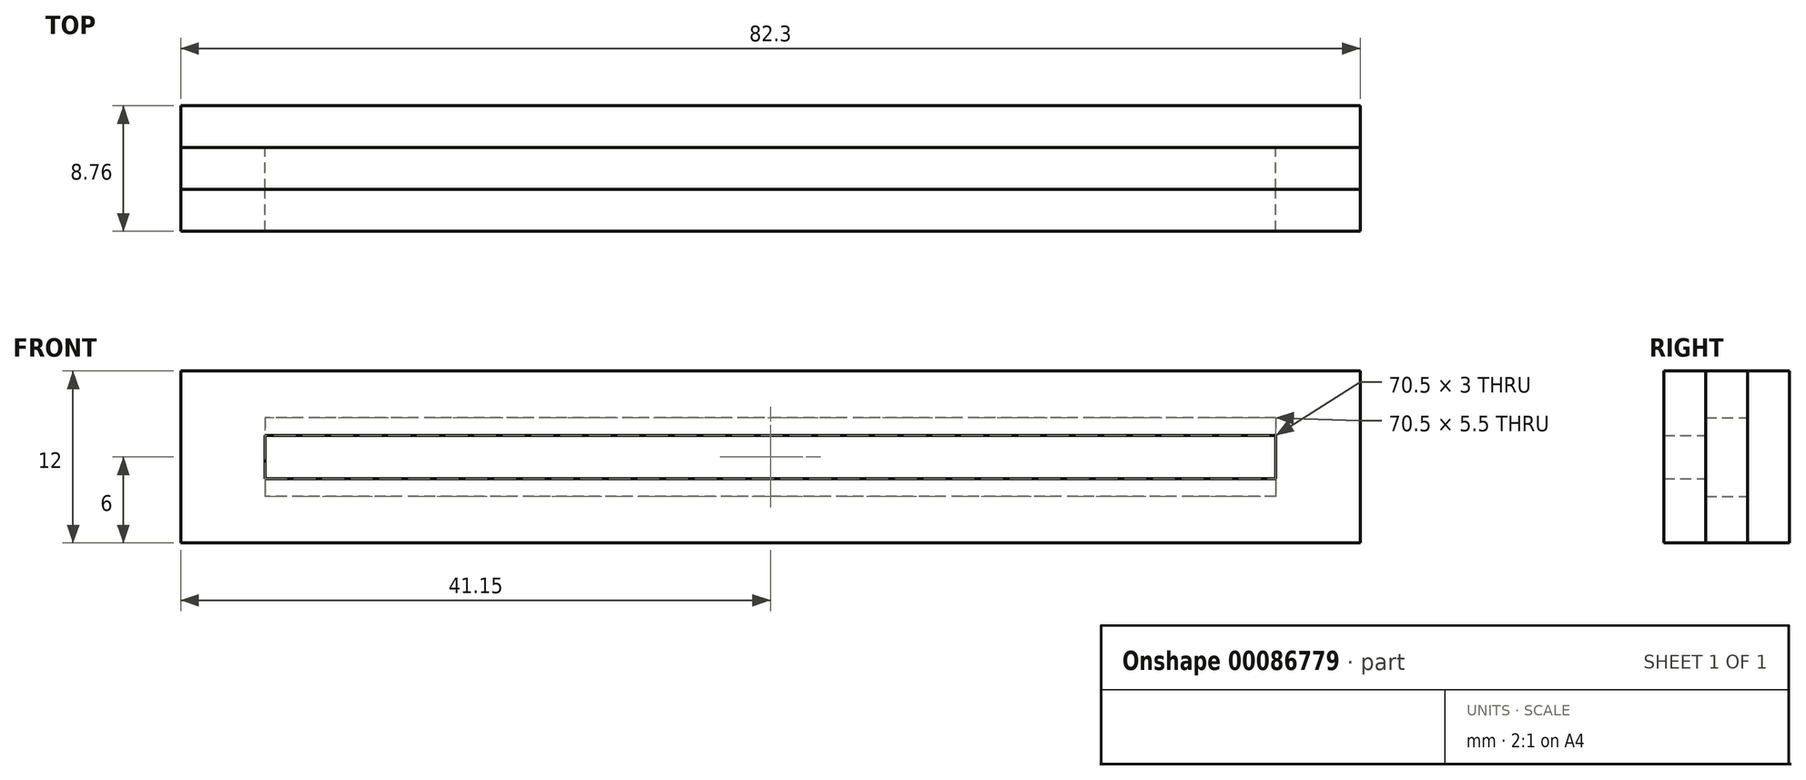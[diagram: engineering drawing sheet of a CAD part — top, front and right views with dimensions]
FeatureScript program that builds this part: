
annotation { "Feature Type Name" : "Feature", "Feature Type Description" : "" }
export const myFeature = defineFeature(function(context is Context, id is Id, definition is map)
    precondition{}
    {
        {
            var Q0;
            Q0=qCreatedBy(makeId("Front.planeOp"),FACE);
            var sketch = newSketch(context, id + "F0", { "sketchPlane" : qUnion([Q0])});
            skLineSegment(sketch, "E0.bottom", {"start": v(41.15, 6) * mm, "end": v(-41.15, 6) * mm});
            skLineSegment(sketch, "E0.top", {"start": v(41.15, -6) * mm, "end": v(-41.15, -6) * mm});
            skLineSegment(sketch, "E0.left", {"start": v(41.15, 6) * mm, "end": v(41.15, -6) * mm});
            skLineSegment(sketch, "E0.right", {"start": v(-41.15, 6) * mm, "end": v(-41.15, -6) * mm});
            skSolve(sketch);
        }
        {
            var Q0;
            {var subQ0=sQuery(id+"F0.wireOp",EDGE,"c4q2wAaf-wQR1-omqj-YX6Q-xsGUEn6AxWBf.bottom");Q0=makeQuery(id+"F0.imprint","IMPRINT",FACE,{"disambiguationData":[TD([[makeQuery(id+"F0.imprint","IMPRINT",EDGE,{"derivedFrom":subQ0}),1.0]])]});}
            var Q1;
            {var subQ0=sQuery(id+"F0.wireOp",EDGE,"c4q2wAaf-wQR1-omqj-YX6Q-xsGUEn6AxWBf.top");Q1=makeQuery(id+"F0.imprint","IMPRINT",FACE,{"disambiguationData":[TD([[makeQuery(id+"F0.imprint","IMPRINT",EDGE,{"derivedFrom":subQ0}),-1.0]])]});}
            var Q2;
            Q2=makeQuery(id+"F0.imprint","IMPRINT",FACE,{"disambiguationData":[TD([[makeQuery(id+"F0.imprint","IMPRINT",EDGE,{"derivedFrom":sQuery(id+"F0.wireOp",EDGE,"E0.bottom")}),1.0]])]});
            var Q3;
            Q3=makeQuery(id+"F0.imprint","IMPRINT",FACE,{"disambiguationData":[TD([[makeQuery(id+"F0.imprint","IMPRINT",EDGE,{"derivedFrom":sQuery(id+"F0.wireOp",EDGE,"rwk2xs3n-fW5y-CHEW-mY1I-GiypznhDuFsC.bottom")}),-1.0]])]});
            extrude(context, id + "F1", {"entities" : qUnion([Q0, Q1, Q2, Q3]), "depth" : 2.92 * mm});
        }
        {
            var Q0;
            Q0=makeQuery(id+"F1.opExtrude","CAP_FACE",FACE,{"disambiguationData":[OSD([sQuery(id+"F0.wireOp",EDGE,"E0.bottom"),sQuery(id+"F0.wireOp",EDGE,"E0.top"),sQuery(id+"F0.wireOp",EDGE,"E0.left"),sQuery(id+"F0.wireOp",EDGE,"E0.right")])],"isStart":false});
            var sketch = newSketch(context, id + "F2", { "sketchPlane" : qUnion([Q0])});
            skLineSegment(sketch, "E1.bottom", {"start": v(35.25, 2.75) * mm, "end": v(-35.25, 2.75) * mm});
            skLineSegment(sketch, "E1.top", {"start": v(35.25, -2.75) * mm, "end": v(-35.25, -2.75) * mm});
            skLineSegment(sketch, "E1.left", {"start": v(35.25, 2.75) * mm, "end": v(35.25, -2.75) * mm});
            skLineSegment(sketch, "E1.right", {"start": v(-35.25, 2.75) * mm, "end": v(-35.25, -2.75) * mm});
            skPoint(sketch, "E1.middle", {"position": v(0, 0) * mm});
            skSolve(sketch);
        }
        {
            var Q0;
            Q0=makeQuery(id+"F2.imprint","IMPRINT",FACE,{"disambiguationData":[TD([[makeQuery(id+"F2.imprint","IMPRINT",EDGE,{"derivedFrom":sQuery(id+"F2.wireOp",EDGE,"E1.bottom")}),-1.0]])]});
            extrude(context, id + "F3", {"entities" : qUnion([Q0]), "depth" : 2.92 * mm});
        }
        {
            var Q0;
            Q0=makeQuery(id+"F3.opExtrude","CAP_FACE",FACE,{"disambiguationData":[OSD([sQuery(id+"F0.wireOp",EDGE,"E0.bottom"),sQuery(id+"F0.wireOp",EDGE,"E0.top"),sQuery(id+"F0.wireOp",EDGE,"E0.left"),sQuery(id+"F0.wireOp",EDGE,"E0.right"),sQuery(id+"F2.wireOp",EDGE,"E1.bottom"),sQuery(id+"F2.wireOp",EDGE,"E1.top"),sQuery(id+"F2.wireOp",EDGE,"E1.left"),sQuery(id+"F2.wireOp",EDGE,"E1.right")])],"isStart":false});
            var sketch = newSketch(context, id + "F4", { "sketchPlane" : qUnion([Q0])});
            skLineSegment(sketch, "E2.bottom", {"start": v(35.25, -1.5) * mm, "end": v(-35.25, -1.5) * mm});
            skLineSegment(sketch, "E2.top", {"start": v(35.25, 1.5) * mm, "end": v(-35.25, 1.5) * mm});
            skLineSegment(sketch, "E2.left", {"start": v(35.25, -1.5) * mm, "end": v(35.25, 1.5) * mm});
            skLineSegment(sketch, "E2.right", {"start": v(-35.25, -1.5) * mm, "end": v(-35.25, 1.5) * mm});
            skPoint(sketch, "E2.middle", {"position": v(0, 0) * mm});
            skSolve(sketch);
        }
        {
            var Q0;
            {var subQ2=sQuery(id+"F4.wireOp",EDGE,"E2.left");Q0=makeQuery(id+"F4.imprint","IMPRINT",FACE,{"disambiguationData":[TD([[makeQuery(id+"F4.imprint","IMPRINT",EDGE,{"derivedFrom":subQ2}),1.0]])]});}
            var Q1;
            {var subQ0=sQuery(id+"F4.wireOp",EDGE,"E2.top");Q1=makeQuery(id+"F4.imprint","IMPRINT",FACE,{"disambiguationData":[TD([[makeQuery(id+"F4.imprint","IMPRINT",EDGE,{"derivedFrom":subQ0}),-1.0]])]});}
            var Q2;
            {var subQ0=sQuery(id+"F4.wireOp",EDGE,"E2.bottom");Q2=makeQuery(id+"F4.imprint","IMPRINT",FACE,{"disambiguationData":[TD([[makeQuery(id+"F4.imprint","IMPRINT",EDGE,{"derivedFrom":subQ0}),1.0]])]});}
            extrude(context, id + "F5", {"entities" : qUnion([Q0, Q1, Q2]), "depth" : 2.92 * mm});
        }
    });
